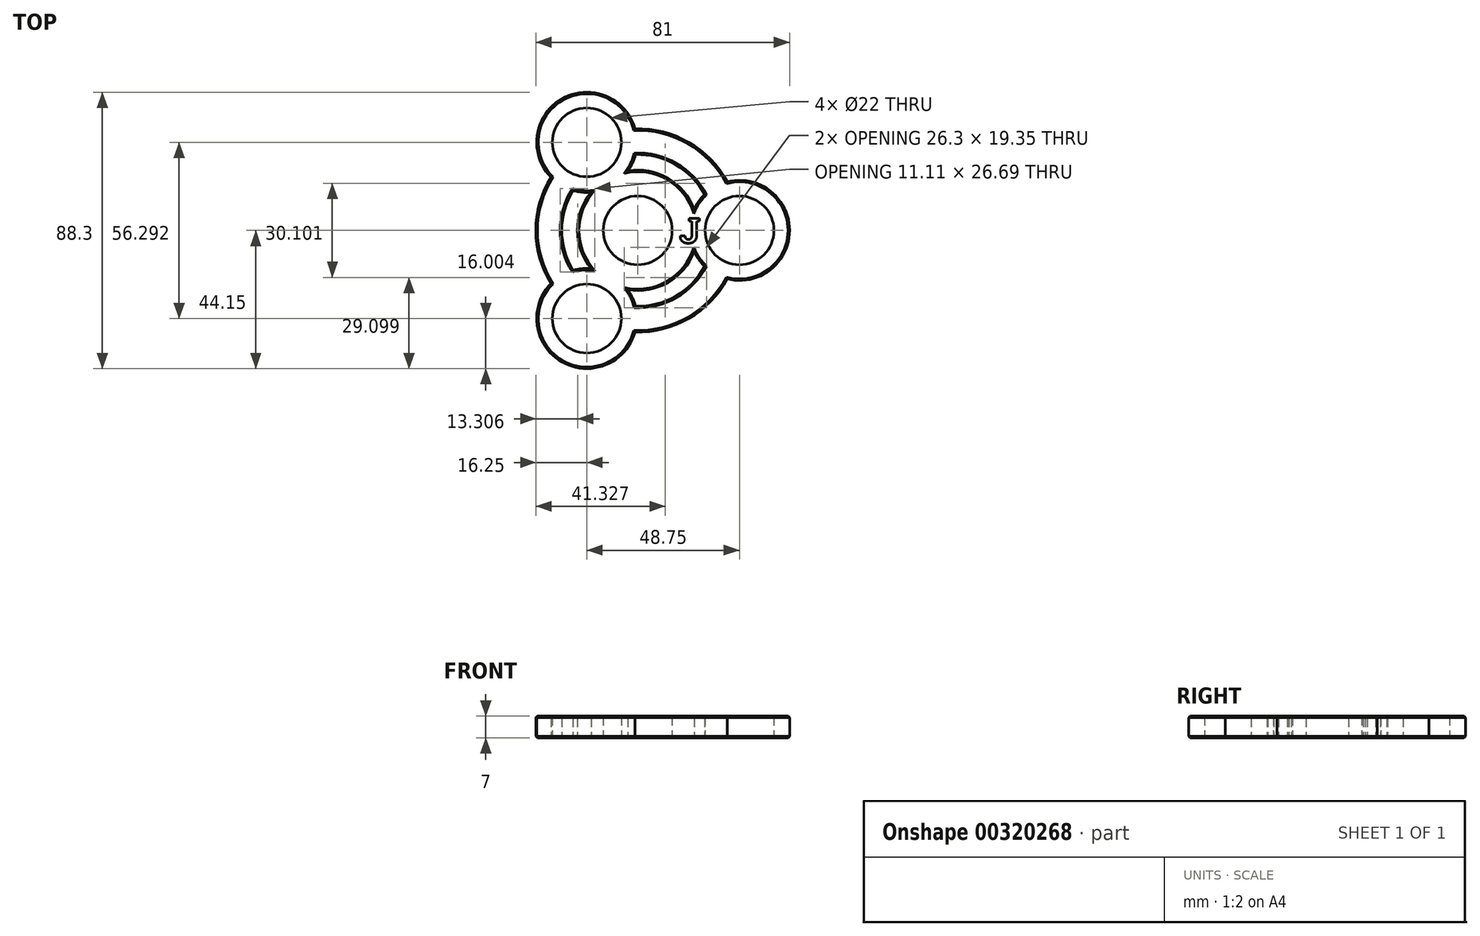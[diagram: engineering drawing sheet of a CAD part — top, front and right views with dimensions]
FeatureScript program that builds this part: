
annotation { "Feature Type Name" : "Feature", "Feature Type Description" : "" }
export const myFeature = defineFeature(function(context is Context, id is Id, definition is map)
    precondition{}
    {
        {
            var Q0;
            Q0=qCreatedBy(makeId("Top.planeOp"),FACE);
            var sketch = newSketch(context, id + "F0", { "sketchPlane" : qUnion([Q0])});
            skCircle(sketch, "E0", {"center": v(0, 0) * mm, "radius": 11 * mm});
            skArc(sketch, "E1", {"start": v(-27.71, 16.98) * mm, "mid": v(-32.5, 0) * mm, "end": v(-27.71, -16.98) * mm});
            skCircle(sketch, "E2", {"center": v(32.5, 0) * mm, "radius": 11 * mm});
            skCircle(sketch, "E3.1.0", {"center": v(-16.25, 28.15) * mm, "radius": 11 * mm});
            skCircle(sketch, "E3.2.0", {"center": v(-16.25, -28.15) * mm, "radius": 11 * mm});
            skArc(sketch, "E4.0", {"start": v(-0.85, 32.49) * mm, "mid": v(-24.25, 42) * mm, "end": v(-27.71, 16.98) * mm});
            skArc(sketch, "E5.0", {"start": v(28.56, -15.5) * mm, "mid": v(48.5, 0) * mm, "end": v(28.56, 15.5) * mm});
            skArc(sketch, "E6.0", {"start": v(-27.71, -16.98) * mm, "mid": v(-24.25, -42) * mm, "end": v(-0.85, -32.49) * mm});
            skArc(sketch, "E7.trimOffspring", {"start": v(28.56, 15.5) * mm, "mid": v(16.25, 28.15) * mm, "end": v(-0.85, 32.49) * mm});
            skArc(sketch, "E8.trimOffspring", {"start": v(-0.85, -32.49) * mm, "mid": v(16.25, -28.15) * mm, "end": v(28.56, -15.5) * mm});
            skArc(sketch, "E9.0", {"start": v(-0.73, -24.24) * mm, "mid": v(12.13, -21) * mm, "end": v(21.36, -11.48) * mm});
            skArc(sketch, "E10.0", {"start": v(-3.13, -19) * mm, "mid": v(9.62, -16.67) * mm, "end": v(18.01, -6.8) * mm});
            skLineSegment(sketch, "E11", {"start": v(-11, 0) * mm, "end": v(-19.25, 0) * mm, "construction": true});
            skLineSegment(sketch, "E12", {"start": v(-24.25, 0) * mm, "end": v(-32.5, 0) * mm, "construction": true});
            skArc(sketch, "E13", {"start": v(-20.62, 12.76) * mm, "mid": v(-17.78, 12.22) * mm, "end": v(-14.89, 12.2) * mm});
            skArc(sketch, "E14", {"start": v(21.36, -11.48) * mm, "mid": v(19.47, -9.29) * mm, "end": v(18.01, -6.8) * mm});
            skArc(sketch, "E15", {"start": v(-20.62, -12.76) * mm, "mid": v(-17.78, -12.22) * mm, "end": v(-14.89, -12.2) * mm});
            skArc(sketch, "E16.trimOffspring", {"start": v(-3.13, -19) * mm, "mid": v(-1.7, -21.5) * mm, "end": v(-0.73, -24.24) * mm});
            skArc(sketch, "E17.trimOffspring", {"start": v(21.36, 11.48) * mm, "mid": v(12.13, 21) * mm, "end": v(-0.73, 24.24) * mm});
            skArc(sketch, "E18.trimOffspring", {"start": v(18.01, 6.8) * mm, "mid": v(9.63, 16.67) * mm, "end": v(-3.13, 19) * mm});
            skArc(sketch, "E19.trimOffspring", {"start": v(18.01, 6.8) * mm, "mid": v(19.47, 9.29) * mm, "end": v(21.36, 11.48) * mm});
            skArc(sketch, "E20.trimOffspring", {"start": v(-20.62, 12.76) * mm, "mid": v(-24.25, 0) * mm, "end": v(-20.62, -12.76) * mm});
            skArc(sketch, "E21.trimOffspring", {"start": v(-14.89, 12.2) * mm, "mid": v(-19.25, 0) * mm, "end": v(-14.89, -12.2) * mm});
            skArc(sketch, "E22.trimOffspring", {"start": v(-3.13, 19) * mm, "mid": v(-1.7, 21.5) * mm, "end": v(-0.73, 24.24) * mm});
            skSolve(sketch);
        }
        {
            var Q0;
            Q0 = qSketchRegion(id + "F0", true);
            extrude(context, id + "F1", {"entities" : qUnion([Q0]), "depth" : 7 * mm});
        }
        {
            var Q0;
            Q0=makeQuery(id+"F1.opExtrude","CAP_EDGE",EDGE,{"disambiguationData":[OSD([sQuery(id+"F0.wireOp",EDGE,"E6.0")])],"isStart":false});
            var Q1;
            Q1=makeQuery(id+"F1.opExtrude","CAP_EDGE",EDGE,{"disambiguationData":[OSD([sQuery(id+"F0.wireOp",EDGE,"E8.trimOffspring")])],"isStart":false});
            var Q2;
            Q2=makeQuery(id+"F1.opExtrude","CAP_EDGE",EDGE,{"disambiguationData":[OSD([sQuery(id+"F0.wireOp",EDGE,"E5.0")])],"isStart":false});
            var Q3;
            Q3=makeQuery(id+"F1.opExtrude","CAP_EDGE",EDGE,{"disambiguationData":[OSD([sQuery(id+"F0.wireOp",EDGE,"E7.trimOffspring")])],"isStart":false});
            var Q4;
            Q4=makeQuery(id+"F1.opExtrude","CAP_EDGE",EDGE,{"disambiguationData":[OSD([sQuery(id+"F0.wireOp",EDGE,"E4.0")])],"isStart":false});
            var Q5;
            Q5=makeQuery(id+"F1.opExtrude","CAP_EDGE",EDGE,{"disambiguationData":[OSD([sQuery(id+"F0.wireOp",EDGE,"E1")])],"isStart":false});
            var Q6;
            Q6=makeQuery(id+"F1.opExtrude","CAP_EDGE",EDGE,{"disambiguationData":[OSD([sQuery(id+"F0.wireOp",EDGE,"E20.trimOffspring")])],"isStart":false});
            var Q7;
            Q7=makeQuery(id+"F1.opExtrude","CAP_EDGE",EDGE,{"disambiguationData":[OSD([sQuery(id+"F0.wireOp",EDGE,"E21.trimOffspring")])],"isStart":false});
            var Q8;
            Q8=makeQuery(id+"F1.opExtrude","CAP_EDGE",EDGE,{"disambiguationData":[OSD([sQuery(id+"F0.wireOp",EDGE,"E13")])],"isStart":false});
            var Q9;
            Q9=makeQuery(id+"F1.opExtrude","CAP_EDGE",EDGE,{"disambiguationData":[OSD([sQuery(id+"F0.wireOp",EDGE,"E15")])],"isStart":false});
            var Q10;
            Q10=makeQuery(id+"F1.opExtrude","CAP_EDGE",EDGE,{"disambiguationData":[OSD([sQuery(id+"F0.wireOp",EDGE,"E9.0")])],"isStart":false});
            var Q11;
            Q11=makeQuery(id+"F1.opExtrude","CAP_EDGE",EDGE,{"disambiguationData":[OSD([sQuery(id+"F0.wireOp",EDGE,"E10.0")])],"isStart":false});
            var Q12;
            Q12=makeQuery(id+"F1.opExtrude","CAP_EDGE",EDGE,{"disambiguationData":[OSD([sQuery(id+"F0.wireOp",EDGE,"E16.trimOffspring")])],"isStart":false});
            var Q13;
            Q13=makeQuery(id+"F1.opExtrude","CAP_EDGE",EDGE,{"disambiguationData":[OSD([sQuery(id+"F0.wireOp",EDGE,"E14")])],"isStart":false});
            var Q14;
            Q14=makeQuery(id+"F1.opExtrude","CAP_EDGE",EDGE,{"disambiguationData":[OSD([sQuery(id+"F0.wireOp",EDGE,"E18.trimOffspring")])],"isStart":false});
            var Q15;
            Q15=makeQuery(id+"F1.opExtrude","CAP_EDGE",EDGE,{"disambiguationData":[OSD([sQuery(id+"F0.wireOp",EDGE,"E17.trimOffspring")])],"isStart":false});
            var Q16;
            Q16=makeQuery(id+"F1.opExtrude","CAP_EDGE",EDGE,{"disambiguationData":[OSD([sQuery(id+"F0.wireOp",EDGE,"E19.trimOffspring")])],"isStart":false});
            var Q17;
            Q17=makeQuery(id+"F1.opExtrude","CAP_EDGE",EDGE,{"disambiguationData":[OSD([sQuery(id+"F0.wireOp",EDGE,"E22.trimOffspring")])],"isStart":false});
            var Q18;
            Q18=makeQuery(id+"F1.opExtrude","CAP_EDGE",EDGE,{"disambiguationData":[OSD([sQuery(id+"F0.wireOp",EDGE,"E21.trimOffspring")])],"isStart":true});
            var Q19;
            Q19=makeQuery(id+"F1.opExtrude","CAP_EDGE",EDGE,{"disambiguationData":[OSD([sQuery(id+"F0.wireOp",EDGE,"E15")])],"isStart":true});
            var Q20;
            Q20=makeQuery(id+"F1.opExtrude","CAP_EDGE",EDGE,{"disambiguationData":[OSD([sQuery(id+"F0.wireOp",EDGE,"E20.trimOffspring")])],"isStart":true});
            var Q21;
            Q21=makeQuery(id+"F1.opExtrude","CAP_EDGE",EDGE,{"disambiguationData":[OSD([sQuery(id+"F0.wireOp",EDGE,"E13")])],"isStart":true});
            var Q22;
            Q22=makeQuery(id+"F1.opExtrude","CAP_EDGE",EDGE,{"disambiguationData":[OSD([sQuery(id+"F0.wireOp",EDGE,"E22.trimOffspring")])],"isStart":true});
            var Q23;
            Q23=makeQuery(id+"F1.opExtrude","CAP_EDGE",EDGE,{"disambiguationData":[OSD([sQuery(id+"F0.wireOp",EDGE,"E17.trimOffspring")])],"isStart":true});
            var Q24;
            Q24=makeQuery(id+"F1.opExtrude","CAP_EDGE",EDGE,{"disambiguationData":[OSD([sQuery(id+"F0.wireOp",EDGE,"E18.trimOffspring")])],"isStart":true});
            var Q25;
            Q25=makeQuery(id+"F1.opExtrude","CAP_EDGE",EDGE,{"disambiguationData":[OSD([sQuery(id+"F0.wireOp",EDGE,"E19.trimOffspring")])],"isStart":true});
            var Q26;
            Q26=makeQuery(id+"F1.opExtrude","CAP_EDGE",EDGE,{"disambiguationData":[OSD([sQuery(id+"F0.wireOp",EDGE,"E14")])],"isStart":true});
            var Q27;
            Q27=makeQuery(id+"F1.opExtrude","CAP_EDGE",EDGE,{"disambiguationData":[OSD([sQuery(id+"F0.wireOp",EDGE,"E10.0")])],"isStart":true});
            var Q28;
            Q28=makeQuery(id+"F1.opExtrude","CAP_EDGE",EDGE,{"disambiguationData":[OSD([sQuery(id+"F0.wireOp",EDGE,"E9.0")])],"isStart":true});
            var Q29;
            Q29=makeQuery(id+"F1.opExtrude","CAP_EDGE",EDGE,{"disambiguationData":[OSD([sQuery(id+"F0.wireOp",EDGE,"E16.trimOffspring")])],"isStart":true});
            var Q30;
            Q30=makeQuery(id+"F1.opExtrude","CAP_EDGE",EDGE,{"disambiguationData":[OSD([sQuery(id+"F0.wireOp",EDGE,"E6.0")])],"isStart":true});
            var Q31;
            Q31=makeQuery(id+"F1.opExtrude","CAP_EDGE",EDGE,{"disambiguationData":[OSD([sQuery(id+"F0.wireOp",EDGE,"E8.trimOffspring")])],"isStart":true});
            var Q32;
            Q32=makeQuery(id+"F1.opExtrude","CAP_EDGE",EDGE,{"disambiguationData":[OSD([sQuery(id+"F0.wireOp",EDGE,"E5.0")])],"isStart":true});
            var Q33;
            Q33=makeQuery(id+"F1.opExtrude","CAP_EDGE",EDGE,{"disambiguationData":[OSD([sQuery(id+"F0.wireOp",EDGE,"E7.trimOffspring")])],"isStart":true});
            var Q34;
            Q34=makeQuery(id+"F1.opExtrude","CAP_EDGE",EDGE,{"disambiguationData":[OSD([sQuery(id+"F0.wireOp",EDGE,"E4.0")])],"isStart":true});
            var Q35;
            Q35=makeQuery(id+"F1.opExtrude","CAP_EDGE",EDGE,{"disambiguationData":[OSD([sQuery(id+"F0.wireOp",EDGE,"E1")])],"isStart":true});
            chamfer(context, id + "F2", {"entities" : qUnion([Q0, Q1, Q2, Q3, Q4, Q5, Q6, Q7, Q8, Q9, Q10, Q11, Q12, Q13, Q14, Q15, Q16, Q17, Q18, Q19, Q20, Q21, Q22, Q23, Q24, Q25, Q26, Q27, Q28, Q29, Q30, Q31, Q32, Q33, Q34, Q35]), "width" : 0.5 * mm, "tangentPropagation" : true});
        }
        {
            var Q0;
            Q0=makeQuery(id+"F1.opExtrude","CAP_FACE",FACE,{"disambiguationData":[OSD([sQuery(id+"F0.wireOp",EDGE,"E0"),sQuery(id+"F0.wireOp",EDGE,"E1"),sQuery(id+"F0.wireOp",EDGE,"E2"),sQuery(id+"F0.wireOp",EDGE,"E3.1.0"),sQuery(id+"F0.wireOp",EDGE,"E3.2.0"),sQuery(id+"F0.wireOp",EDGE,"E4.0"),sQuery(id+"F0.wireOp",EDGE,"E5.0"),sQuery(id+"F0.wireOp",EDGE,"E6.0"),sQuery(id+"F0.wireOp",EDGE,"E7.trimOffspring"),sQuery(id+"F0.wireOp",EDGE,"E8.trimOffspring"),sQuery(id+"F0.wireOp",EDGE,"E9.0"),sQuery(id+"F0.wireOp",EDGE,"E10.0"),sQuery(id+"F0.wireOp",EDGE,"E13"),sQuery(id+"F0.wireOp",EDGE,"E14"),sQuery(id+"F0.wireOp",EDGE,"E15"),sQuery(id+"F0.wireOp",EDGE,"E16.trimOffspring"),sQuery(id+"F0.wireOp",EDGE,"E17.trimOffspring"),sQuery(id+"F0.wireOp",EDGE,"E18.trimOffspring"),sQuery(id+"F0.wireOp",EDGE,"E19.trimOffspring"),sQuery(id+"F0.wireOp",EDGE,"E20.trimOffspring"),sQuery(id+"F0.wireOp",EDGE,"E21.trimOffspring"),sQuery(id+"F0.wireOp",EDGE,"E22.trimOffspring")])],"isStart":false});
            var sketch = newSketch(context, id + "F3", { "sketchPlane" : qUnion([Q0])});
            skText(sketch, "E23", { "text": "J", "fontName": "RobotoSlab-Bold.ttf"});
            skPoint(sketch, "E24", {"position": v(13.36, 0) * mm});
            const initialGuessF3  = {"E23": [0.01336, -0.004, 1, 0, 0.008]};
            skSetInitialGuess(sketch, initialGuessF3);
            skSolve(sketch);
        }
        {
            var Q0;
            Q0=makeQuery(id+"F3.imprint","IMPRINT",FACE,{"disambiguationData":[TD([[makeQuery(id+"F3.imprint","IMPRINT",EDGE,{"derivedFrom":sQuery(id+"F3.wireOp",EDGE,"E23.sketch_text.stroke-0")}),-1.0]])]});
            extrude(context, id + "F4", {"entities" : qUnion([Q0]), "operationType" : NewBodyOperationType.REMOVE, "oppositeDirection" : true, "depth" : 0.5 * mm});
        }
    });
